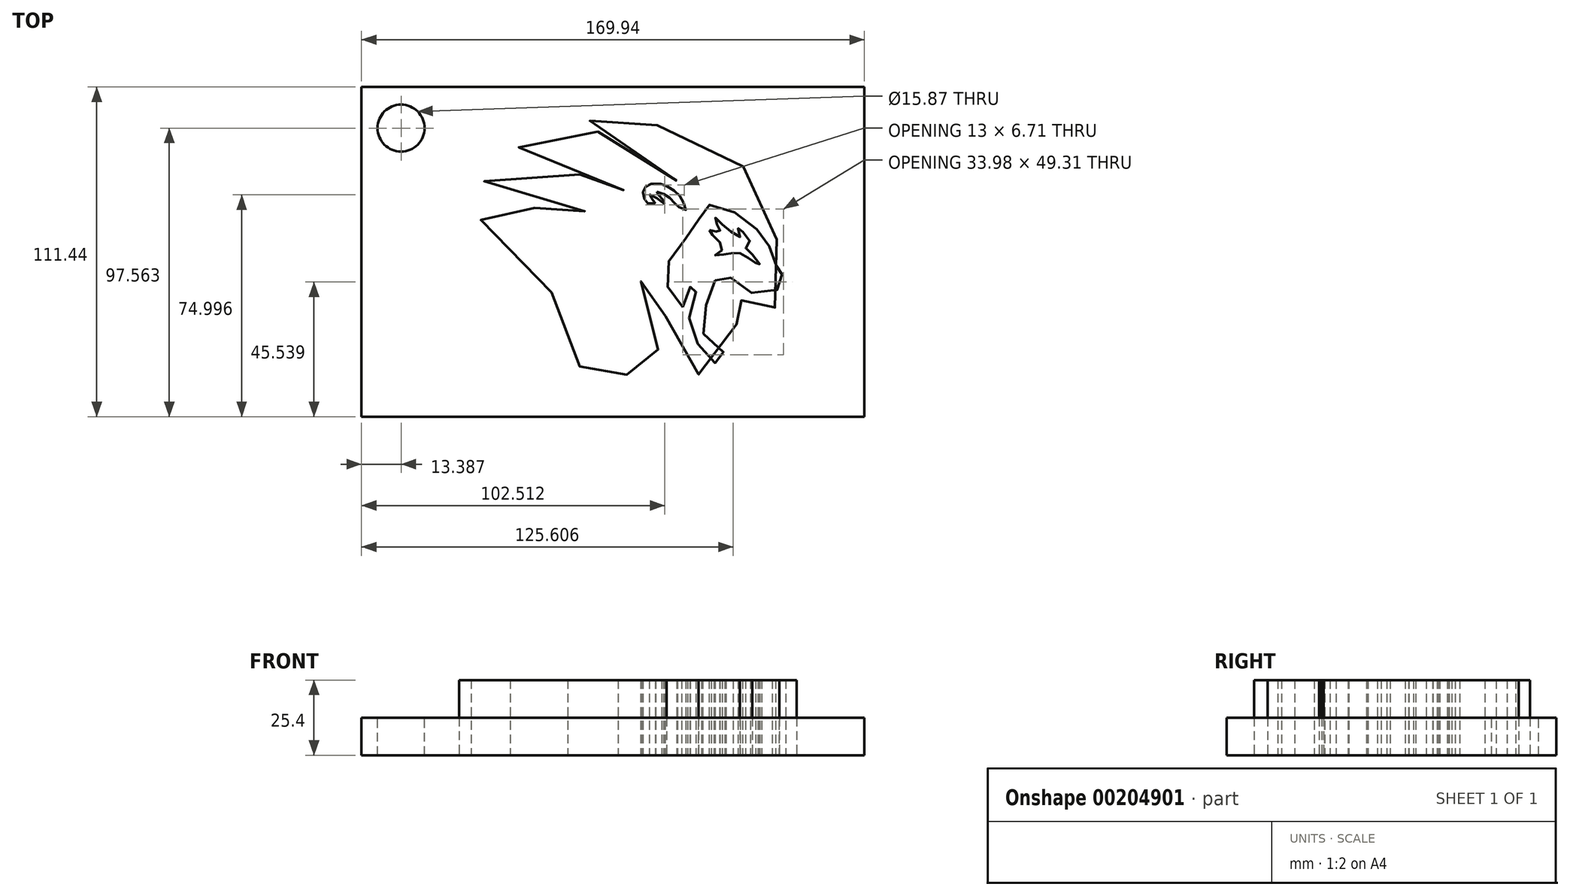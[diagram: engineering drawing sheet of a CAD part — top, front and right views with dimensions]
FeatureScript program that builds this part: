
annotation { "Feature Type Name" : "Feature", "Feature Type Description" : "" }
export const myFeature = defineFeature(function(context is Context, id is Id, definition is map)
    precondition{}
    {
        {
            var Q0;
            Q0=qCreatedBy(makeId("Top.planeOp"),FACE);
            var sketch = newSketch(context, id + "F0", { "sketchPlane" : qUnion([Q0])});
            skFitSpline(sketch, "E0", {"points": [v(-14.87, -19.96) * mm, v(-16.53, -17.13) * mm, v(-18.86, -13.58) * mm, v(-21.78, -9.61) * mm, v(-24.55, -6.73) * mm, v(-29.24, -2.2) * mm, v(-33.32, 1.06) * mm, v(-37.46, 3.8) * mm, v(-40.9, 5.46) * mm, v(-43.35, 6.3) * mm, v(-45.8, 6.8) * mm, v(-46.1, 7) * mm, v(-45.1, 7.59) * mm, v(-39.68, 8.6) * mm, v(-34.05, 9.1) * mm, v(-26.3, 9.07) * mm, v(-20, 8.52) * mm, v(-11.98, 6.95) * mm, v(-2.95, 4.5) * mm, v(7.46, -0.37) * mm, v(7.58, -0.43) * mm, v(5.39, 1.58) * mm, v(1.22, 4.64) * mm, v(-6.3, 8.72) * mm, v(-13.47, 10.97) * mm, v(-20.35, 12.54) * mm, v(-32.07, 13.18) * mm, v(-42.1, 12.72) * mm, v(-42, 12.83) * mm, v(-37.72, 17.5) * mm, v(-31.7, 23.1) * mm, v(-29.15, 25.2) * mm, v(-24.9, 25.08) * mm, v(-20.47, 24.47) * mm, v(-15.32, 23.36) * mm, v(-11.1, 22.1) * mm, v(-6, 20.24) * mm, v(-1.72, 18.52) * mm, v(2.27, 16.6) * mm, v(8.16, 13.3) * mm, v(13.4, 9.63) * mm, v(15.68, 7.8) * mm, v(15.68, 7.82) * mm, v(14.13, 9.77) * mm, v(12.1, 12.08) * mm, v(8.3, 15.63) * mm, v(5.1, 18.14) * mm, v(0.78, 20.85) * mm, v(-6.8, 24.67) * mm, v(-16.6, 27.67) * mm, v(-19.8, 28.49) * mm, v(-23.88, 28.93) * mm, v(-27.84, 29.13) * mm, v(-28.83, 29.25) * mm, v(-28.25, 30.03) * mm, v(-24.92, 31.85) * mm, v(-18.83, 34.06) * mm, v(-13.56, 35.28) * mm, v(-9.07, 35.69) * mm, v(-3.03, 35.3) * mm, v(3.32, 33.44) * mm, v(8.22, 31.43) * mm, v(14.57, 27.73) * mm, v(19.8, 23.97) * mm, v(25.5, 18.58) * mm, v(29.06, 15.28) * mm, v(29.06, 15.31) * mm, v(27.98, 16.94) * mm, v(25.97, 19.45) * mm, v(22.94, 23.1) * mm, v(19.59, 26.07) * mm, v(16.79, 28.66) * mm, v(12.12, 32.04) * mm, v(7.7, 34.26) * mm, v(0, 37.44) * mm, v(-4.46, 38.57) * mm, v(-9.33, 39.6) * mm, v(-9.3, 39.74) * mm, v(-7.35, 40.32) * mm, v(1.8, 40.56) * mm, v(8.65, 39.94) * mm, v(15.65, 38.31) * mm, v(20.75, 36.65) * mm, v(27.72, 32.86) * mm, v(27.72, 32.89) * mm, v(27.46, 36.7) * mm, v(27.52, 36.77) * mm, v(31.83, 34.93) * mm, v(36.67, 32.57) * mm, v(42.64, 28.75) * mm, v(48.48, 24.06) * mm, v(52.7, 18.98) * mm, v(54.89, 13.8) * mm, v(55.33, 9.69) * mm, v(55.18, 7.18) * mm, v(55.27, 7.1) * mm, v(57.42, 4.85) * mm, v(60.51, 1.35) * mm, v(61.91, -0.72) * mm, v(61.88, -0.8) * mm, v(60.78, -1.71) * mm, v(60.9, -1.8) * mm, v(63.2, -4.3) * mm, v(66.14, -7.78) * mm, v(67.85, -11.11) * mm, v(67.85, -13.12) * mm, v(67.46, -14.96) * mm, v(65.54, -18.66) * mm, v(63.46, -20.9) * mm, v(62.06, -22.18) * mm, v(62.03, -22.43) * mm, v(60.9, -24.65) * mm, v(58.62, -26.9) * mm, v(55.24, -28.88) * mm, v(52.93, -29.11) * mm, v(52.9, -28.97) * mm, v(54.07, -26.96) * mm, v(53.95, -27.07) * mm, v(52.2, -28.1) * mm, v(50.31, -28.74) * mm, v(46.46, -28.82) * mm, v(46.5, -28.65) * mm, v(49.67, -22.96) * mm, v(49.32, -22.67) * mm, v(48.18, -21.97) * mm, v(47.13, -20.96) * mm, v(47.05, -20.96) * mm, v(46.7, -21.42) * mm, v(45.15, -23.14) * mm, v(44.22, -23.85) * mm, v(44.1, -24.19) * mm, v(44.19, -29.7) * mm, v(44.22, -29.7) * mm, v(44.92, -28.76) * mm, v(44.95, -28.8) * mm, v(45.44, -29.35) * mm, v(45.8, -30.37) * mm, v(45.9, -32.23) * mm, v(46, -32.23) * mm, v(47.48, -30.69) * mm, v(47.54, -30.69) * mm, v(47.98, -31.21) * mm, v(48.42, -32.87) * mm, v(48.68, -36.43) * mm, v(47.54, -38.62) * mm, v(47.37, -39.43) * mm, v(46.46, -42.26) * mm, v(44.66, -45.2) * mm, v(41.97, -47.1) * mm, v(38.65, -48.03) * mm, v(34.77, -47.92) * mm, v(34.74, -47.86) * mm, v(36.17, -45.32) * mm, v(36.17, -45.26) * mm, v(34.07, -43.66) * mm, v(30.98, -41.07) * mm, v(29.12, -39.32) * mm, v(27.14, -36.66) * mm, v(26.2, -34.83) * mm, v(25.45, -32.87) * mm, v(24.9, -30.05) * mm, v(24.75, -28.85) * mm, v(24.66, -28.8) * mm, v(23.29, -27.54) * mm, v(21.74, -25.69) * mm, v(20.52, -23.85) * mm, v(18.68, -20.22) * mm, v(17.37, -17.45) * mm, v(16.55, -14.63) * mm, v(15.91, -12.2) * mm, v(15.77, -9.76) * mm, v(15.68, -9.76) * mm, v(15.36, -12.64) * mm, v(15.27, -16.23) * mm, v(16.12, -20.1) * mm, v(17.46, -23.43) * mm, v(19.24, -26.14) * mm, v(22.06, -29.32) * mm, v(22.27, -29.52) * mm, v(22.3, -30.95) * mm, v(22.73, -33.22) * mm, v(23.96, -35.85) * mm, v(23.93, -36) * mm, v(22.82, -36.98) * mm, v(20.93, -39.55) * mm, v(19.88, -41.24) * mm, v(19.24, -43.28) * mm, v(19.1, -43.4) * mm, v(18.57, -43.08) * mm, v(17.87, -42.17) * mm, v(17.08, -41.15) * mm, v(16.06, -39.6) * mm, v(15.65, -38.9) * mm, v(15.62, -38.94) * mm, v(14.51, -40.3) * mm, v(13.32, -42.03) * mm, v(11.95, -44.27) * mm, v(11.07, -46.34) * mm, v(10.35, -48.41) * mm, v(9.62, -50.86) * mm, v(9.35, -52.58) * mm, v(9.3, -52.58) * mm, v(7.52, -52.23) * mm, v(6.06, -51.74) * mm, v(4.14, -50.95) * mm, v(2.62, -50.28) * mm, v(0.46, -49.2) * mm, v(-0.88, -48.32) * mm, v(-2.69, -47.13) * mm, v(-4.06, -46.14) * mm, v(-5.37, -45) * mm, v(-6.5, -43.86) * mm, v(-7.09, -43.08) * mm, v(-7.35, -41.82) * mm, v(-7.58, -39.96) * mm, v(-8.43, -37.07) * mm, v(-9.27, -34.13) * mm, v(-10.79, -29.55) * mm, v(-12.22, -25.9) * mm, v(-14.26, -21.53) * mm, v(-14.87, -19.96) * mm]});
            skFitSpline(sketch, "E1", {"points": [v(20.64, 14.12) * mm, v(21.76, 13.88) * mm, v(23.17, 13.2) * mm, v(24.26, 12.5) * mm, v(25.27, 11.74) * mm, v(26.44, 10.52) * mm, v(27.07, 9.84) * mm, v(27.64, 9.1) * mm, v(27.7, 9.06) * mm, v(30.4, 7.75) * mm, v(30.5, 7.73) * mm, v(30.46, 7.97) * mm, v(30.13, 9) * mm, v(29.51, 10.69) * mm, v(28.86, 12.03) * mm, v(27.76, 13.35) * mm, v(26.8, 14.2) * mm, v(25.54, 15.12) * mm, v(24.24, 15.9) * mm, v(23, 16.5) * mm, v(21.47, 16.84) * mm, v(19.08, 16.75) * mm, v(17.8, 16.44) * mm, v(16.92, 15.9) * mm, v(16.42, 15.22) * mm, v(16.11, 14.43) * mm, v(15.98, 12.98) * mm, v(16.3, 11.89) * mm, v(16.76, 11.13) * mm, v(17.4, 10.34) * mm, v(17.5, 10.21) * mm, v(20.2, 10.12) * mm, v(20.2, 10.16) * mm, v(20, 10.47) * mm, v(19.46, 11.3) * mm, v(18.95, 11.9) * mm, v(18.42, 12.67) * mm, v(18.18, 13.08) * mm, v(18.18, 13.1) * mm, v(18.77, 12.97) * mm, v(20.42, 12.07) * mm, v(21.6, 11.22) * mm, v(23.34, 10) * mm, v(23.4, 10.01) * mm, v(23.45, 10.34) * mm, v(22.77, 11.31) * mm, v(21.82, 12.43) * mm, v(21.06, 13.19) * mm, v(20.47, 13.8) * mm, v(20.36, 14.07) * mm, v(20.64, 14.12) * mm]});
            skFitSpline(sketch, "E2", {"points": [v(29.5, -24.96) * mm, v(28.58, -24.35) * mm, v(27.6, -23.28) * mm, v(26.55, -21.99) * mm, v(25.54, -20.52) * mm, v(24.7, -18.86) * mm, v(23.88, -16.81) * mm, v(23.47, -15.09) * mm, v(22.99, -12.75) * mm, v(23.1, -12.53) * mm, v(23.95, -10.91) * mm, v(24.86, -9.04) * mm, v(25.75, -7.35) * mm, v(26.7, -5.8) * mm, v(27.88, -4.41) * mm, v(29.43, -2.66) * mm, v(31.27, -0.9) * mm, v(33.27, 0.81) * mm, v(35.98, 3.21) * mm, v(35.98, 3.28) * mm, v(35.63, 3.76) * mm, v(35.07, 4.35) * mm, v(34.8, 4.96) * mm, v(34.63, 5.81) * mm, v(34.7, 7.06) * mm, v(34.93, 7.73) * mm, v(35.94, 8.78) * mm, v(36.81, 9.33) * mm, v(38.01, 9.61) * mm, v(39.35, 9.66) * mm, v(40.85, 9.42) * mm, v(42.3, 9.1) * mm, v(43.98, 8.55) * mm, v(45.84, 7.68) * mm, v(47.83, 6.54) * mm, v(49.9, 5.2) * mm, v(51.6, 3.98) * mm, v(52.98, 2.8) * mm, v(53.93, 1.93) * mm, v(55, 0.77) * mm, v(56.05, -0.54) * mm, v(56.03, -0.56) * mm, v(54.91, -1.2) * mm, v(56.03, -2.2) * mm, v(57.65, -3.42) * mm, v(59.34, -4.88) * mm, v(61.47, -7.1) * mm, v(63.04, -8.9) * mm, v(64.22, -10.48) * mm, v(64.2, -10.5) * mm, v(59.74, -11.02) * mm, v(59.72, -11.02) * mm, v(59.74, -11.42) * mm, v(59.9, -11.48) * mm, v(60.57, -11.75) * mm, v(62.04, -12.36) * mm, v(62.65, -12.6) * mm, v(62.67, -12.62) * mm, v(62.71, -13.34) * mm, v(62.89, -13.71) * mm, v(63.48, -14.6) * mm, v(64.22, -15.52) * mm, v(64.24, -15.74) * mm, v(63.94, -16.3) * mm, v(63.43, -17) * mm, v(62.73, -17.9) * mm, v(61.93, -18.67) * mm, v(60.8, -19.43) * mm, v(59.6, -19.98) * mm, v(58.43, -20.37) * mm, v(57.17, -20.61) * mm, v(54.26, -20.46) * mm, v(52.54, -20.04) * mm, v(51.49, -19.56) * mm, v(49.87, -18.62) * mm, v(48.5, -17.51) * mm, v(47.3, -16.44) * mm, v(45.88, -15.17) * mm, v(44.76, -14.52) * mm, v(44.04, -14.3) * mm, v(41.64, -14.17) * mm, v(40.04, -14.54) * mm, v(39.04, -15.41) * mm, v(39.08, -15.44) * mm, v(41.8, -16.57) * mm, v(41.82, -16.65) * mm, v(40.93, -18) * mm, v(39.82, -19.8) * mm, v(38.1, -22.76) * mm, v(36.88, -24.94) * mm, v(36.12, -27.16) * mm, v(35.87, -29.14) * mm, v(35.87, -32.06) * mm, v(36.24, -33.32) * mm, v(37, -35.08) * mm, v(38.26, -36.67) * mm, v(39.49, -37.84) * mm, v(41.2, -39.1) * mm, v(42.76, -39.92) * mm, v(43.55, -40.27) * mm, v(43.61, -40.33) * mm, v(43.34, -41.19) * mm, v(42.78, -42.37) * mm, v(41.7, -43.5) * mm, v(39.96, -44.59) * mm, v(39.96, -44.57) * mm, v(40.25, -43.87) * mm, v(40.3, -43.77) * mm, v(39.86, -43.27) * mm, v(38.83, -42.37) * mm, v(37.58, -41.13) * mm, v(36.04, -39.4) * mm, v(34.86, -37.76) * mm, v(33.78, -36.12) * mm, v(32.58, -33.71) * mm, v(31.7, -31.43) * mm, v(31.06, -29.18) * mm, v(31.06, -29.1) * mm, v(31.73, -28.48) * mm, v(32.62, -26.8) * mm, v(33.3, -25.15) * mm, v(33.67, -23.64) * mm, v(33.9, -21.67) * mm, v(33.87, -19.43) * mm, v(33.67, -17.84) * mm, v(33.1, -16.36) * mm, v(31.92, -14.6) * mm, v(31.92, -14.67) * mm, v(31.88, -16.13) * mm, v(31.92, -18.77) * mm, v(31.78, -19.78) * mm, v(31.5, -21.26) * mm, v(31.1, -22.48) * mm, v(30.62, -23.69) * mm, v(29.88, -24.82) * mm, v(29.5, -24.96) * mm]});
            skFitSpline(sketch, "E3", {"points": [v(38.42, 1.18) * mm, v(39.29, 1.15) * mm, v(40.25, 0.8) * mm, v(41.21, 0.31) * mm, v(41.88, -0.27) * mm, v(42, 1.04) * mm, v(41.85, 1.4) * mm, v(41.47, 2.15) * mm, v(40.8, 3.44) * mm, v(40.14, 5.4) * mm, v(40.27, 5.48) * mm, v(40.92, 4.71) * mm, v(42.09, 3.55) * mm, v(43.78, 2.2) * mm, v(45.64, 0.72) * mm, v(48.76, -1.62) * mm, v(48.65, -0.59) * mm, v(48.35, 0.81) * mm, v(48.14, 1.88) * mm, v(48.27, 1.95) * mm, v(49.02, 1.25) * mm, v(50, 0.31) * mm, v(51.08, -1) * mm, v(52.33, -3.64) * mm, v(51.05, -4.61) * mm, v(50.7, -5.43) * mm, v(52.05, -6.37) * mm, v(54, -8.43) * mm, v(55.42, -10.4) * mm, v(55.36, -10.94) * mm, v(54.7, -10.56) * mm, v(53.66, -9.71) * mm, v(52.53, -8.9) * mm, v(51.42, -8.2) * mm, v(50.02, -7.38) * mm, v(48.75, -6.77) * mm, v(48.26, -6.65) * mm, v(47.4, -6.6) * mm, v(46.02, -6.65) * mm, v(44.24, -6.89) * mm, v(42.3, -7.38) * mm, v(40.41, -7.78) * mm, v(40.83, -6.76) * mm, v(42.29, -6.14) * mm, v(42.68, -5.5) * mm, v(42.64, -4.48) * mm, v(42.09, -3.21) * mm, v(40.68, -1.57) * mm, v(39.33, -0.38) * mm, v(38.62, 0.45) * mm, v(38.42, 0.86) * mm, v(38.42, 1.18) * mm]});
            skFitSpline(sketch, "E4.0", {"points": [v(-37, 28.67) * mm, v(-36.89, 28.92) * mm, v(-36.76, 29.16) * mm, v(-36.57, 29.48) * mm, v(-36.3, 29.86) * mm, v(-35.9, 30.24) * mm, v(-35.52, 30.53) * mm, v(-35.17, 30.74) * mm, v(-34.88, 30.9) * mm, v(-34.64, 31) * mm, v(-34.44, 31.1) * mm, v(-34.26, 31.2) * mm, v(-34.04, 31.32) * mm, v(-33.79, 31.47) * mm, v(-33.42, 31.7) * mm, v(-32.9, 32.04) * mm, v(-32.2, 32.49) * mm, v(-31.46, 32.97) * mm, v(-30.66, 33.45) * mm, v(-29.97, 33.85) * mm, v(-29.4, 34.16) * mm, v(-28.83, 34.46) * mm, v(-28.13, 34.78) * mm, v(-27.05, 35.24) * mm, v(-26.05, 35.64) * mm, v(-25.09, 36.06) * mm, v(-24.38, 36.4) * mm, v(-23.78, 36.72) * mm, v(-23.3, 37.01) * mm, v(-22.8, 37.33) * mm, v(-22.15, 37.79) * mm, v(-21.3, 38.43) * mm, v(-20.43, 39.12) * mm, v(-19.53, 39.85) * mm, v(-18.62, 40.6) * mm, v(-17.7, 41.32) * mm, v(-16.79, 42.02) * mm, v(-16.02, 42.56) * mm, v(-15.4, 42.95) * mm, v(-14.93, 43.23) * mm, v(-14.45, 43.48) * mm, v(-13.78, 43.79) * mm, v(-12.97, 44.06) * mm, v(-12.06, 44.25) * mm, v(-11.23, 44.33) * mm, v(-10.64, 44.35) * mm, v(-10.23, 44.35) * mm, v(-9.95, 44.35) * mm, v(-9.7, 44.36) * mm, v(-9.4, 44.37) * mm, v(-9, 44.4) * mm, v(-8.49, 44.45) * mm, v(-7.94, 44.52) * mm, v(-7.35, 44.6) * mm, v(-6.82, 44.66) * mm, v(-6.38, 44.7) * mm, v(-5.72, 44.77) * mm, v(-4.7, 44.85) * mm, v(-3.3, 44.93) * mm, v(-1.81, 45) * mm, v(-0.24, 45.06) * mm, v(1.39, 45.1) * mm, v(2.74, 45.1) * mm, v(3.8, 45.08) * mm, v(4.82, 45.04) * mm, v(6.04, 44.95) * mm, v(7.23, 44.85) * mm, v(8.19, 44.76) * mm, v(9.17, 44.67) * mm, v(10.2, 44.57) * mm, v(11.21, 44.46) * mm, v(11.95, 44.36) * mm, v(12.54, 44.27) * mm, v(13, 44.18) * mm, v(13.34, 44.1) * mm, v(13.65, 44.03) * mm, v(14.02, 43.93) * mm, v(14.41, 43.81) * mm, v(14.8, 43.7) * mm, v(15.15, 43.62) * mm, v(15.47, 43.57) * mm, v(15.84, 43.52) * mm, v(16.44, 43.45) * mm, v(17.33, 43.4) * mm, v(18.33, 43.35) * mm, v(19.41, 43.3) * mm, v(20.92, 43.25) * mm, v(22.47, 43.18) * mm, v(23.95, 43.07) * mm, v(25, 42.96) * mm, v(26, 42.82) * mm, v(26.89, 42.63) * mm, v(27.7, 42.41) * mm, v(28.43, 42.17) * mm, v(29.1, 41.91) * mm, v(29.64, 41.7) * mm, v(30.05, 41.52) * mm, v(30.46, 41.35) * mm, v(31, 41.13) * mm, v(31.7, 40.85) * mm, v(32.67, 40.45) * mm, v(33.69, 40.03) * mm, v(34.7, 39.6) * mm, v(35.45, 39.26) * mm, v(36.17, 38.92) * mm, v(37.09, 38.47) * mm, v(38.15, 37.91) * mm, v(39.13, 37.39) * mm, v(39.87, 36.99) * mm, v(40.6, 36.6) * mm, v(41.53, 36.1) * mm, v(42.66, 35.5) * mm, v(43.81, 34.85) * mm, v(44.77, 34.25) * mm, v(45.54, 33.75) * mm, v(46.1, 33.36) * mm, v(46.66, 32.94) * mm, v(47.18, 32.54) * mm, v(47.67, 32.14) * mm, v(48.15, 31.75) * mm, v(48.62, 31.37) * mm, v(49, 31.07) * mm, v(49.31, 30.84) * mm, v(49.64, 30.6) * mm, v(50.06, 30.29) * mm, v(50.6, 29.88) * mm, v(51.17, 29.45) * mm, v(51.65, 29.05) * mm, v(52.04, 28.7) * mm, v(52.33, 28.42) * mm, v(52.61, 28.13) * mm, v(52.97, 27.75) * mm, v(53.38, 27.27) * mm, v(53.83, 26.7) * mm, v(54.25, 26.15) * mm, v(54.63, 25.65) * mm, v(54.93, 25.26) * mm, v(55.15, 24.99) * mm, v(55.38, 24.71) * mm, v(55.68, 24.37) * mm, v(56.05, 23.94) * mm, v(56.44, 23.49) * mm, v(56.83, 23) * mm, v(57.23, 22.46) * mm, v(57.6, 21.9) * mm, v(58.06, 21.15) * mm, v(58.57, 20.18) * mm, v(59.13, 18.98) * mm, v(59.62, 17.76) * mm, v(59.98, 16.77) * mm, v(60.23, 16.02) * mm, v(60.45, 15.29) * mm, v(60.7, 14.37) * mm, v(61.06, 13.09) * mm, v(61.53, 11.43) * mm, v(62, 9.95) * mm, v(62.37, 8.83) * mm, v(62.65, 8.05) * mm, v(62.88, 7.5) * mm, v(63.05, 7.13) * mm, v(63.16, 6.9) * mm, v(63.26, 6.73) * mm, v(63.38, 6.53) * mm, v(63.52, 6.34) * mm, v(63.72, 6.1) * mm, v(63.96, 5.84) * mm, v(64.2, 5.58) * mm, v(64.46, 5.28) * mm, v(64.79, 4.88) * mm, v(65.19, 4.37) * mm, v(65.59, 3.84) * mm, v(65.99, 3.28) * mm, v(66.39, 2.7) * mm, v(66.78, 2.12) * mm, v(67.16, 1.55) * mm, v(67.51, 1) * mm, v(67.84, 0.49) * mm, v(68.11, 0.03) * mm, v(68.34, -0.36) * mm, v(68.51, -0.67) * mm, v(68.65, -0.92) * mm, v(68.8, -1.2) * mm, v(69.07, -1.66) * mm, v(69.4, -2.22) * mm, v(69.79, -2.85) * mm, v(70.2, -3.51) * mm, v(70.61, -4.17) * mm, v(71.01, -4.79) * mm, v(71.37, -5.32) * mm, v(71.68, -5.77) * mm, v(71.97, -6.16) * mm, v(72.24, -6.53) * mm, v(72.54, -6.9) * mm, v(72.85, -7.3) * mm, v(73.24, -7.8) * mm, v(73.65, -8.36) * mm, v(74.06, -9.02) * mm, v(74.38, -9.66) * mm, v(74.6, -10.22) * mm, v(74.72, -10.6) * mm, v(74.8, -10.92) * mm, v(74.87, -11.22) * mm, v(74.92, -11.6) * mm, v(74.96, -12.03) * mm, v(74.99, -12.59) * mm, v(74.97, -13.24) * mm, v(74.9, -13.92) * mm, v(74.84, -14.4) * mm, v(74.79, -14.72) * mm, v(74.74, -15.02) * mm, v(74.67, -15.4) * mm, v(74.58, -15.8) * mm, v(74.48, -16.12) * mm, v(74.36, -16.45) * mm, v(74.21, -16.83) * mm, v(74.03, -17.26) * mm, v(73.87, -17.61) * mm, v(73.76, -17.88) * mm, v(73.64, -18.15) * mm, v(73.49, -18.53) * mm, v(73.27, -19.04) * mm, v(73.06, -19.5) * mm, v(72.85, -19.88) * mm, v(72.68, -20.17) * mm, v(72.48, -20.47) * mm, v(72.28, -20.73) * mm, v(72.09, -20.97) * mm, v(71.85, -21.24) * mm, v(71.63, -21.47) * mm, v(71.47, -21.65) * mm, v(71.38, -21.75) * mm, v(71.33, -21.81) * mm, v(71.27, -21.88) * mm, v(71.2, -21.98) * mm, v(71.09, -22.1) * mm, v(70.94, -22.3) * mm, v(70.76, -22.54) * mm, v(70.54, -22.8) * mm, v(70.36, -23.02) * mm, v(70.17, -23.22) * mm, v(69.93, -23.47) * mm, v(69.62, -23.76) * mm, v(69.34, -24.02) * mm, v(69.13, -24.22) * mm, v(68.99, -24.35) * mm, v(68.84, -24.5) * mm, v(68.64, -24.68) * mm, v(68.37, -24.94) * mm, v(68.06, -25.21) * mm, v(67.8, -25.44) * mm, v(67.5, -25.67) * mm, v(67.18, -25.9) * mm, v(66.91, -26.11) * mm, v(66.75, -26.24) * mm, v(66.66, -26.32) * mm, v(66.6, -26.37) * mm, v(66.6, -26.38) * mm, v(66.59, -26.4) * mm, v(66.56, -26.44) * mm, v(66.5, -26.52) * mm, v(66.43, -26.64) * mm, v(66.33, -26.82) * mm, v(66.22, -27) * mm, v(66.1, -27.15) * mm, v(66, -27.3) * mm, v(65.88, -27.49) * mm, v(65.72, -27.7) * mm, v(65.52, -27.95) * mm, v(65.28, -28.26) * mm, v(65.06, -28.54) * mm, v(64.92, -28.73) * mm, v(64.81, -28.9) * mm, v(64.7, -29.07) * mm, v(64.52, -29.32) * mm, v(64.27, -29.68) * mm, v(63.97, -30.05) * mm, v(63.74, -30.3) * mm, v(63.58, -30.47) * mm, v(63.37, -30.67) * mm, v(63.12, -30.89) * mm, v(62.78, -31.15) * mm, v(62.38, -31.44) * mm, v(61.98, -31.7) * mm, v(61.68, -31.89) * mm, v(61.47, -32.02) * mm, v(61.25, -32.16) * mm, v(60.94, -32.35) * mm, v(60.52, -32.6) * mm, v(60.06, -32.85) * mm, v(59.67, -33.04) * mm, v(59.35, -33.18) * mm, v(59.08, -33.28) * mm, v(58.85, -33.36) * mm, v(58.63, -33.43) * mm, v(58.38, -33.5) * mm, v(58.02, -33.6) * mm, v(57.65, -33.69) * mm, v(57.3, -33.79) * mm, v(57.06, -33.89) * mm, v(56.87, -33.99) * mm, v(56.7, -34.08) * mm, v(56.52, -34.21) * mm, v(56.24, -34.41) * mm, v(55.88, -34.72) * mm, v(55.45, -35.15) * mm, v(55.06, -35.61) * mm, v(54.74, -36.06) * mm, v(54.55, -36.4) * mm, v(54.46, -36.62) * mm, v(54.38, -36.84) * mm, v(54.3, -37.13) * mm, v(54.24, -37.55) * mm, v(54.2, -37.99) * mm, v(54.16, -38.39) * mm, v(54.13, -38.71) * mm, v(54.1, -39.01) * mm, v(54.05, -39.26) * mm, v(54, -39.52) * mm, v(53.93, -39.84) * mm, v(53.8, -40.32) * mm, v(53.62, -40.89) * mm, v(53.38, -41.51) * mm, v(53.14, -42.1) * mm, v(52.96, -42.55) * mm, v(52.82, -42.9) * mm, v(52.69, -43.27) * mm, v(52.51, -43.77) * mm, v(52.28, -44.43) * mm, v(52.02, -45.13) * mm, v(51.7, -45.87) * mm, v(51.38, -46.5) * mm, v(51.08, -47.02) * mm, v(50.75, -47.53) * mm, v(50.3, -48.12) * mm, v(49.7, -48.78) * mm, v(48.85, -49.58) * mm, v(47.72, -50.46) * mm, v(46.3, -51.35) * mm, v(44.83, -52.1) * mm, v(43.35, -52.7) * mm, v(41.9, -53.15) * mm, v(40.51, -53.43) * mm, v(39.39, -53.55) * mm, v(38.61, -53.58) * mm, v(38.17, -53.59) * mm, v(37.71, -53.6) * mm, v(37.13, -53.58) * mm, v(36.41, -53.53) * mm, v(35.8, -53.45) * mm, v(35.3, -53.36) * mm, v(34.93, -53.27) * mm, v(34.62, -53.18) * mm, v(34.36, -53.1) * mm, v(34.13, -53) * mm, v(33.87, -52.9) * mm, v(33.52, -52.74) * mm, v(33.22, -52.6) * mm, v(32.99, -52.53) * mm, v(32.78, -52.5) * mm, v(32.53, -52.48) * mm, v(32.3, -52.48) * mm, v(31.98, -52.5) * mm, v(31.58, -52.56) * mm, v(31.1, -52.65) * mm, v(30.4, -52.8) * mm, v(29.38, -53.06) * mm, v(27.54, -53.58) * mm, v(24.94, -54.4) * mm, v(21.58, -55.49) * mm, v(18.76, -56.35) * mm, v(16.6, -56.93) * mm, v(15.03, -57.29) * mm, v(13.78, -57.52) * mm, v(12.83, -57.64) * mm, v(12.13, -57.7) * mm, v(11.45, -57.72) * mm, v(10.6, -57.69) * mm, v(9.63, -57.57) * mm, v(8.63, -57.32) * mm, v(7.95, -57.08) * mm, v(7.5, -56.88) * mm, v(7.2, -56.75) * mm, v(6.97, -56.63) * mm, v(6.82, -56.56) * mm, v(6.75, -56.53) * mm, v(6.72, -56.51) * mm, v(6.7, -56.5) * mm, v(6.69, -56.5) * mm, v(6.67, -56.5) * mm, v(6.57, -56.47) * mm, v(6.33, -56.41) * mm, v(6.03, -56.32) * mm, v(5.83, -56.26) * mm, v(5.64, -56.2) * mm, v(5.38, -56.1) * mm, v(4.96, -55.95) * mm, v(4.4, -55.74) * mm, v(3.72, -55.47) * mm, v(3.18, -55.27) * mm, v(2.78, -55.12) * mm, v(2.52, -55.03) * mm, v(2.33, -54.97) * mm, v(2.21, -54.94) * mm, v(2.11, -54.91) * mm, v(2, -54.88) * mm, v(1.87, -54.86) * mm, v(1.7, -54.82) * mm, v(1.49, -54.78) * mm, v(1.22, -54.72) * mm, v(0.95, -54.64) * mm, v(0.72, -54.55) * mm, v(0.5, -54.46) * mm, v(0.27, -54.34) * mm, v(0.01, -54.2) * mm, v(-0.3, -54.01) * mm, v(-0.65, -53.79) * mm, v(-0.96, -53.59) * mm, v(-1.17, -53.45) * mm, v(-1.4, -53.32) * mm, v(-1.71, -53.14) * mm, v(-2.12, -52.91) * mm, v(-2.56, -52.66) * mm, v(-3.18, -52.28) * mm, v(-3.75, -51.9) * mm, v(-4.2, -51.58) * mm, v(-4.46, -51.41) * mm, v(-4.64, -51.3) * mm, v(-4.82, -51.17) * mm, v(-5.07, -51) * mm, v(-5.54, -50.69) * mm, v(-6.16, -50.24) * mm, v(-6.85, -49.67) * mm, v(-7.36, -49.21) * mm, v(-7.85, -48.74) * mm, v(-8.32, -48.28) * mm, v(-8.68, -47.9) * mm, v(-8.93, -47.63) * mm, v(-9.1, -47.43) * mm, v(-9.29, -47.22) * mm, v(-9.53, -46.92) * mm, v(-9.83, -46.47) * mm, v(-10.07, -45.96) * mm, v(-10.22, -45.55) * mm, v(-10.35, -45.16) * mm, v(-10.48, -44.67) * mm, v(-10.62, -44.07) * mm, v(-10.75, -43.45) * mm, v(-10.89, -42.83) * mm, v(-11.02, -42.23) * mm, v(-11.22, -41.42) * mm, v(-11.5, -40.38) * mm, v(-11.79, -39.32) * mm, v(-12.03, -38.45) * mm, v(-12.27, -37.6) * mm, v(-12.58, -36.54) * mm, v(-12.97, -35.3) * mm, v(-13.42, -34.11) * mm, v(-13.88, -33.06) * mm, v(-14.24, -32.23) * mm, v(-14.5, -31.62) * mm, v(-14.76, -31.02) * mm, v(-15.06, -30.24) * mm, v(-15.28, -29.59) * mm, v(-15.48, -29) * mm, v(-15.6, -28.64) * mm, v(-15.72, -28.33) * mm, v(-15.85, -28) * mm, v(-16.04, -27.54) * mm, v(-16.3, -26.96) * mm, v(-16.56, -26.36) * mm, v(-16.83, -25.77) * mm, v(-17.1, -25.18) * mm, v(-17.36, -24.64) * mm, v(-17.7, -23.96) * mm, v(-18.1, -23.18) * mm, v(-18.62, -22.23) * mm, v(-19.27, -21.16) * mm, v(-20.03, -20) * mm, v(-20.71, -18.96) * mm, v(-21.28, -18.1) * mm, v(-21.85, -17.25) * mm, v(-22.42, -16.4) * mm, v(-22.98, -15.6) * mm, v(-23.4, -15.03) * mm, v(-23.8, -14.5) * mm, v(-24.31, -13.84) * mm, v(-24.96, -13.07) * mm, v(-25.6, -12.34) * mm, v(-26.06, -11.82) * mm, v(-26.33, -11.5) * mm, v(-26.72, -11.06) * mm, v(-27.29, -10.4) * mm, v(-27.97, -9.64) * mm, v(-28.58, -9) * mm, v(-29.1, -8.5) * mm, v(-29.67, -7.95) * mm, v(-30.47, -7.2) * mm, v(-31.3, -6.46) * mm, v(-32.1, -5.75) * mm, v(-32.65, -5.26) * mm, v(-33.17, -4.8) * mm, v(-33.61, -4.42) * mm, v(-34.01, -4.08) * mm, v(-34.38, -3.78) * mm, v(-34.76, -3.5) * mm, v(-35.18, -3.2) * mm, v(-35.68, -2.89) * mm, v(-36.44, -2.43) * mm, v(-37.54, -1.81) * mm, v(-38.93, -1.06) * mm, v(-40.3, -0.33) * mm, v(-41.29, 0.18) * mm, v(-42, 0.52) * mm, v(-42.5, 0.74) * mm, v(-42.98, 0.92) * mm, v(-43.41, 1.05) * mm, v(-43.93, 1.18) * mm, v(-44.52, 1.32) * mm, v(-45.19, 1.48) * mm, v(-45.93, 1.7) * mm, v(-46.73, 1.99) * mm, v(-47.58, 2.38) * mm, v(-48.41, 2.85) * mm, v(-49.23, 3.41) * mm, v(-49.87, 3.97) * mm, v(-50.34, 4.51) * mm, v(-50.68, 4.98) * mm, v(-50.97, 5.52) * mm, v(-51.16, 6.07) * mm, v(-51.24, 6.57) * mm, v(-51.26, 6.97) * mm, v(-51.24, 7.35) * mm, v(-51.15, 7.84) * mm, v(-50.96, 8.38) * mm, v(-50.68, 8.9) * mm, v(-50.37, 9.34) * mm, v(-49.95, 9.83) * mm, v(-49.42, 10.34) * mm, v(-48.83, 10.86) * mm, v(-48.4, 11.23) * mm, v(-48.13, 11.49) * mm, v(-47.93, 11.68) * mm, v(-47.74, 11.88) * mm, v(-47.5, 12.16) * mm, v(-47.2, 12.51) * mm, v(-46.83, 12.97) * mm, v(-46.45, 13.47) * mm, v(-46.03, 14) * mm, v(-45.43, 14.77) * mm, v(-44.76, 15.54) * mm, v(-44.04, 16.32) * mm, v(-43.46, 16.9) * mm, v(-42.85, 17.47) * mm, v(-42.31, 17.95) * mm, v(-41.87, 18.31) * mm, v(-41.43, 18.66) * mm, v(-40.91, 19.07) * mm, v(-40.34, 19.54) * mm, v(-39.82, 20) * mm, v(-39.38, 20.44) * mm, v(-39, 20.9) * mm, v(-38.74, 21.29) * mm, v(-38.57, 21.63) * mm, v(-38.4, 22) * mm, v(-38.22, 22.56) * mm, v(-38.02, 23.38) * mm, v(-37.86, 24.27) * mm, v(-37.71, 25.21) * mm, v(-37.58, 26.15) * mm, v(-37.46, 26.92) * mm, v(-37.34, 27.52) * mm, v(-37.23, 27.97) * mm, v(-37.11, 28.36) * mm, v(-37, 28.67) * mm, v(-36.89, 28.92) * mm, v(-36.76, 29.16) * mm, v(-37, 28.67) * mm]});
            skSolve(sketch);
        }
        {
            var Q0;
            Q0=makeQuery(id+"F0.imprint","IMPRINT",FACE,{"disambiguationData":[TD([[makeQuery(id+"F0.imprint","IMPRINT",EDGE,{"derivedFrom":sQuery(id+"F0.wireOp",EDGE,"E0")}),-1.0]])]});
            var Q1;
            Q1=makeQuery(id+"F0.imprint","IMPRINT",FACE,{"disambiguationData":[TD([[makeQuery(id+"F0.imprint","IMPRINT",EDGE,{"derivedFrom":sQuery(id+"F0.wireOp",EDGE,"E3")}),-1.0]])]});
            extrude(context, id + "F1", {"entities" : qUnion([Q0, Q1]), "depth" : 25.4 * mm});
        }
        {
            var Q0;
            Q0=qCreatedBy(makeId("Top.planeOp"),FACE);
            var sketch = newSketch(context, id + "F2", { "sketchPlane" : qUnion([Q0])});
            skLineSegment(sketch, "E5.bottom", {"start": v(-79.12, 49.47) * mm, "end": v(90.82, 49.47) * mm});
            skLineSegment(sketch, "E5.top", {"start": v(-79.12, -61.97) * mm, "end": v(90.82, -61.97) * mm});
            skLineSegment(sketch, "E5.left", {"start": v(-79.12, 49.47) * mm, "end": v(-79.12, -61.97) * mm});
            skLineSegment(sketch, "E5.right", {"start": v(90.82, 49.47) * mm, "end": v(90.82, -61.97) * mm});
            skSolve(sketch);
        }
        {
            var Q0;
            Q0=makeQuery(id+"F2.imprint","IMPRINT",FACE,{"disambiguationData":[TD([[makeQuery(id+"F2.imprint","IMPRINT",EDGE,{"derivedFrom":sQuery(id+"F2.wireOp",EDGE,"E5.bottom")}),-1.0]])]});
            extrude(context, id + "F3", {"entities" : qUnion([Q0]), "depth" : 12.7 * mm});
        }
        {
            var Q0;
            Q0=makeQuery(id+"F3.opExtrude","CAP_FACE",FACE,{"disambiguationData":[OSD([sQuery(id+"F2.wireOp",EDGE,"E5.bottom"),sQuery(id+"F2.wireOp",EDGE,"E5.top"),sQuery(id+"F2.wireOp",EDGE,"E5.left"),sQuery(id+"F2.wireOp",EDGE,"E5.right")])],"isStart":false});
            var sketch = newSketch(context, id + "F4", { "sketchPlane" : qUnion([Q0])});
            skCircle(sketch, "E6", {"center": v(-65.73, 35.6) * mm, "radius": 7.93 * mm});
            skSolve(sketch);
        }
        {
            var Q0;
            Q0=makeQuery(id+"F4.imprint","IMPRINT",FACE,{"disambiguationData":[TD([[makeQuery(id+"F4.imprint","IMPRINT",EDGE,{"derivedFrom":sQuery(id+"F4.wireOp",EDGE,"E6")}),1.0]])]});
            extrude(context, id + "F5", {"entities" : qUnion([Q0]), "operationType" : NewBodyOperationType.REMOVE, "endBound" : BoundingType.SYMMETRIC, "oppositeDirection" : true, "depth" : 25.4 * mm});
        }
    });
